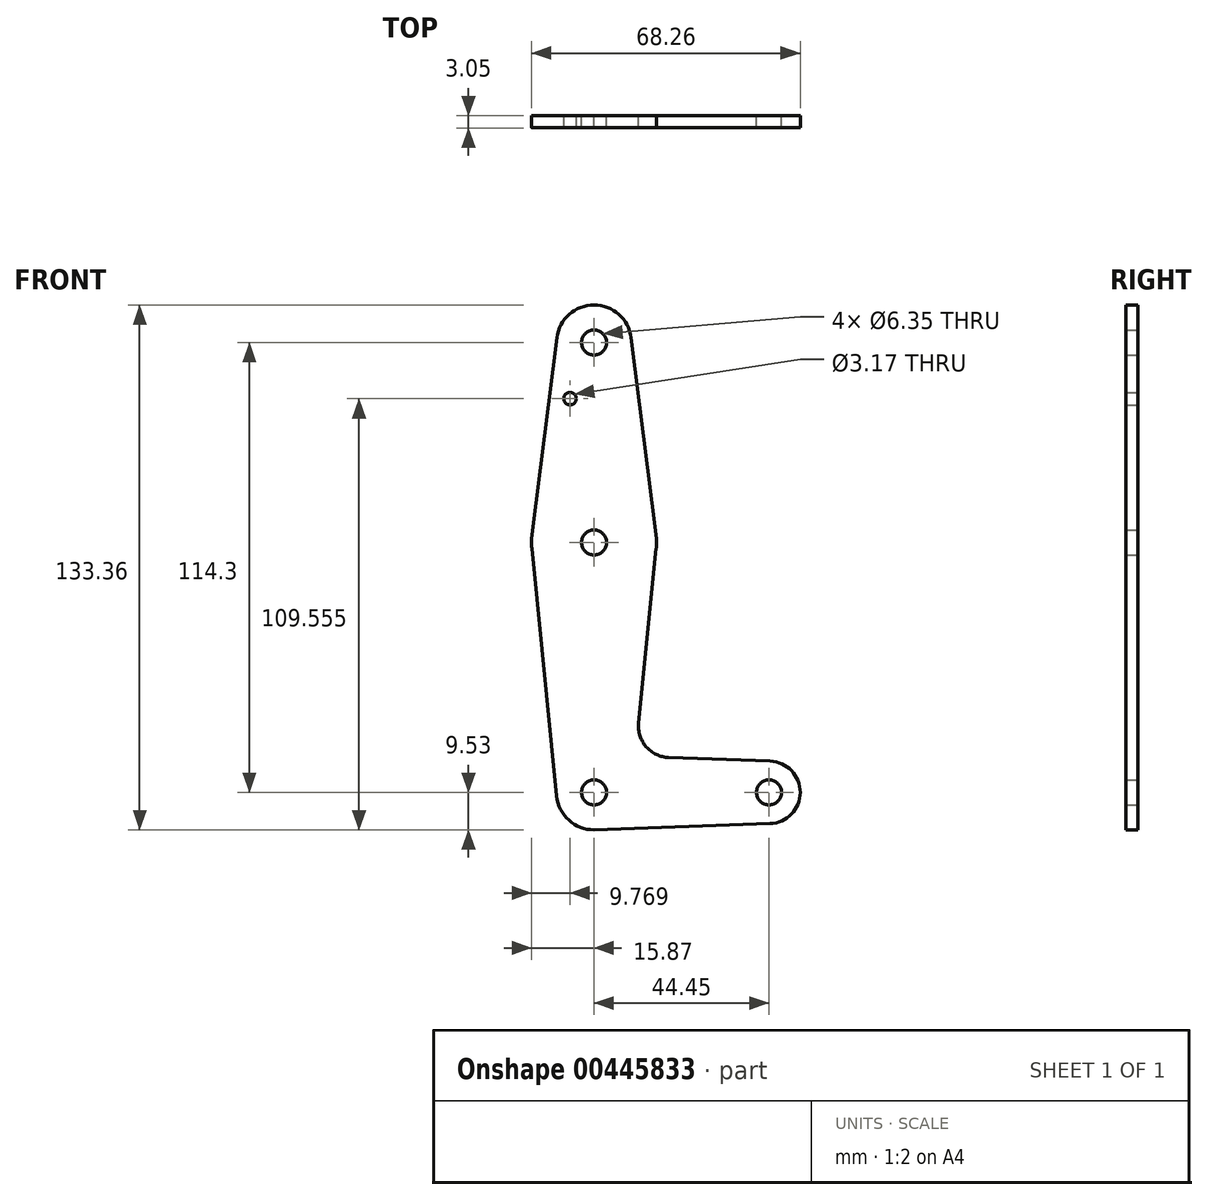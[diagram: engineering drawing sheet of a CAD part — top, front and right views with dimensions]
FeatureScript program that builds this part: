
annotation { "Feature Type Name" : "Feature", "Feature Type Description" : "" }
export const myFeature = defineFeature(function(context is Context, id is Id, definition is map)
    precondition{}
    {
        {
            var Q0;
            Q0=qCreatedBy(makeId("Front.planeOp"),FACE);
            var sketch = newSketch(context, id + "F0", { "sketchPlane" : qUnion([Q0])});
            skLineSegment(sketch, "E0", {"start": v(0, 0) * mm, "end": v(0, 114.3) * mm, "construction": true});
            skLineSegment(sketch, "E1", {"start": v(0, 0) * mm, "end": v(44.45, 0) * mm, "construction": true});
            skCircle(sketch, "E2", {"center": v(0, 0) * mm, "radius": 9.53 * mm});
            skCircle(sketch, "E3", {"center": v(0, 114.3) * mm, "radius": 9.53 * mm});
            skCircle(sketch, "E4", {"center": v(44.45, 0) * mm, "radius": 7.94 * mm});
            skCircle(sketch, "E5", {"center": v(0, 63.5) * mm, "radius": 15.88 * mm});
            skLineSegment(sketch, "E6", {"start": v(9.45, 115.5) * mm, "end": v(15.75, 65.48) * mm});
            skLineSegment(sketch, "E7", {"start": v(-9.45, 115.5) * mm, "end": v(-15.75, 65.48) * mm});
            skCircle(sketch, "E8", {"center": v(0, 0) * mm, "radius": 3.18 * mm});
            skCircle(sketch, "E9", {"center": v(44.45, 0) * mm, "radius": 3.18 * mm});
            skCircle(sketch, "E10", {"center": v(0, 63.5) * mm, "radius": 3.18 * mm});
            skCircle(sketch, "E11", {"center": v(0, 114.3) * mm, "radius": 3.18 * mm});
            skCircle(sketch, "E12", {"center": v(-6.1, 100.03) * mm, "radius": 1.59 * mm});
            skLineSegment(sketch, "E13", {"start": v(0, -9.53) * mm, "end": v(44.73, -7.93) * mm});
            skLineSegment(sketch, "E14", {"start": v(15.8, 61.91) * mm, "end": v(11.34, 17.6) * mm});
            skLineSegment(sketch, "E15", {"start": v(44.73, 7.93) * mm, "end": v(18.97, 8.85) * mm});
            skLineSegment(sketch, "E16", {"start": v(-15.8, 61.91) * mm, "end": v(-9.48, -0.95) * mm});
            skArc(sketch, "E17.filletArc", {"start": v(11.34, 17.6) * mm, "mid": v(13.26, 11.57) * mm, "end": v(18.97, 8.85) * mm});
            skSolve(sketch);
        }
        {
            var Q0;
            {var subQ0=sQuery(id+"F0.wireOp",EDGE,"E13");var subQ1=sQuery(id+"F0.wireOp",EDGE,"E2");var subQ2=makeQuery(id+"F0.imprint","INTERSECT",VERTEX,{"disambiguationData":[OD(0.0)],"derivedFrom":[subQ1,subQ0]});Q0=makeQuery(id+"F0.imprint","IMPRINT",FACE,{"disambiguationData":[TD([[makeQuery(id+"F0.imprint","IMPRINT",EDGE,{"disambiguationData":[TD([[subQ2,-1.0]])],"derivedFrom":subQ1}),1.0]])]});}
            var Q1;
            Q1=makeQuery(id+"F0.imprint","IMPRINT",FACE,{"disambiguationData":[TD([[makeQuery(id+"F0.imprint","IMPRINT",EDGE,{"derivedFrom":sQuery(id+"F0.wireOp",EDGE,"E11")}),-1.0]])]});
            var Q2;
            Q2=makeQuery(id+"F0.imprint","IMPRINT",FACE,{"disambiguationData":[TD([[makeQuery(id+"F0.imprint","IMPRINT",EDGE,{"derivedFrom":sQuery(id+"F0.wireOp",EDGE,"E9")}),-1.0]])]});
            var Q3;
            Q3=makeQuery(id+"F0.imprint","IMPRINT",FACE,{"disambiguationData":[TD([[makeQuery(id+"F0.imprint","IMPRINT",EDGE,{"derivedFrom":sQuery(id+"F0.wireOp",EDGE,"E8")}),-1.0]])]});
            var Q4;
            {var subQ5=sQuery(id+"F0.wireOp",EDGE,"E14");Q4=makeQuery(id+"F0.imprint","IMPRINT",FACE,{"disambiguationData":[TD([[makeQuery(id+"F0.imprint","IMPRINT",EDGE,{"derivedFrom":subQ5}),-1.0]])]});}
            var Q5;
            Q5=makeQuery(id+"F0.imprint","IMPRINT",FACE,{"disambiguationData":[TD([[makeQuery(id+"F0.imprint","IMPRINT",EDGE,{"derivedFrom":sQuery(id+"F0.wireOp",EDGE,"E10")}),-1.0]])]});
            var Q6;
            {var subQ0=sQuery(id+"F0.wireOp",EDGE,"E6");Q6=makeQuery(id+"F0.imprint","IMPRINT",FACE,{"disambiguationData":[TD([[makeQuery(id+"F0.imprint","IMPRINT",EDGE,{"derivedFrom":subQ0}),-1.0]])]});}
            extrude(context, id + "F1", {"entities" : qUnion([Q0, Q1, Q2, Q3, Q4, Q5, Q6]), "depth" : 3.05 * mm});
        }
    });
